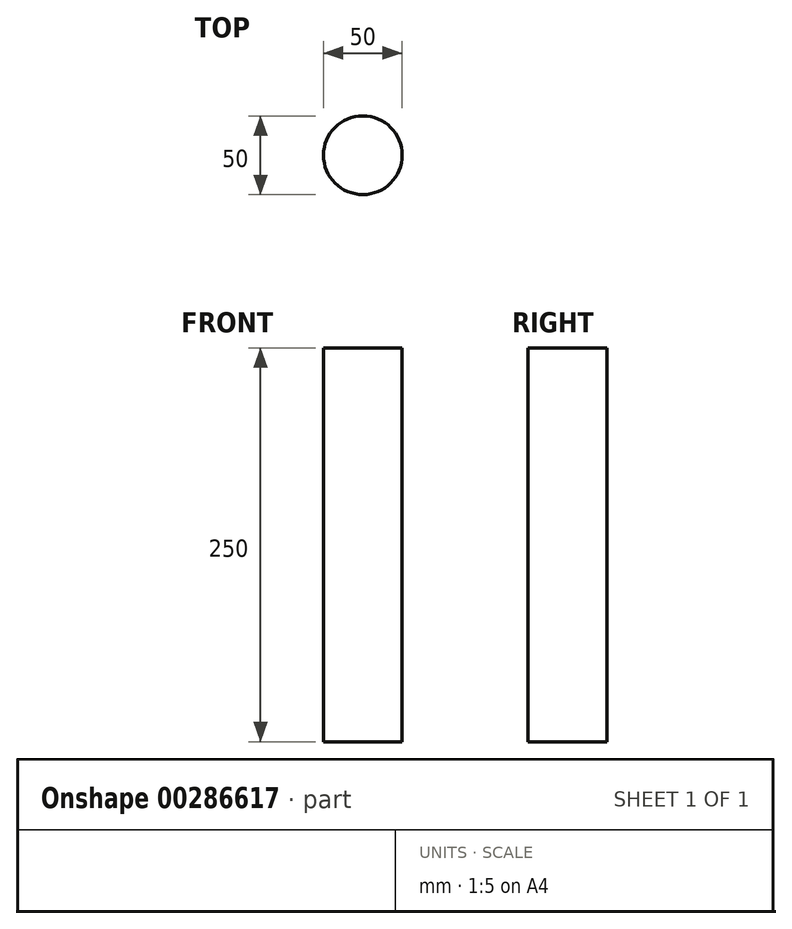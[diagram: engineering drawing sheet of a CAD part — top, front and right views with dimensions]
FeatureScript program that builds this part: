
annotation { "Feature Type Name" : "Feature", "Feature Type Description" : "" }
export const myFeature = defineFeature(function(context is Context, id is Id, definition is map)
    precondition{}
    {
        {
            var Q0;
            Q0=qCreatedBy(makeId("Top.planeOp"),FACE);
            var sketch = newSketch(context, id + "F0", { "sketchPlane" : qUnion([Q0])});
            skCircle(sketch, "E0", {"center": v(0, 0) * mm, "radius": 25 * mm});
            skSolve(sketch);
        }
        {
            var Q0;
            Q0=makeQuery(id+"F0.imprint","IMPRINT",FACE,{"disambiguationData":[TD([[makeQuery(id+"F0.imprint","IMPRINT",EDGE,{"derivedFrom":sQuery(id+"F0.wireOp",EDGE,"E0")}),1.0]])]});
            extrude(context, id + "F1", {"entities" : qUnion([Q0]), "depth" : 250 * mm, "symmetric" : true});
        }
    });
